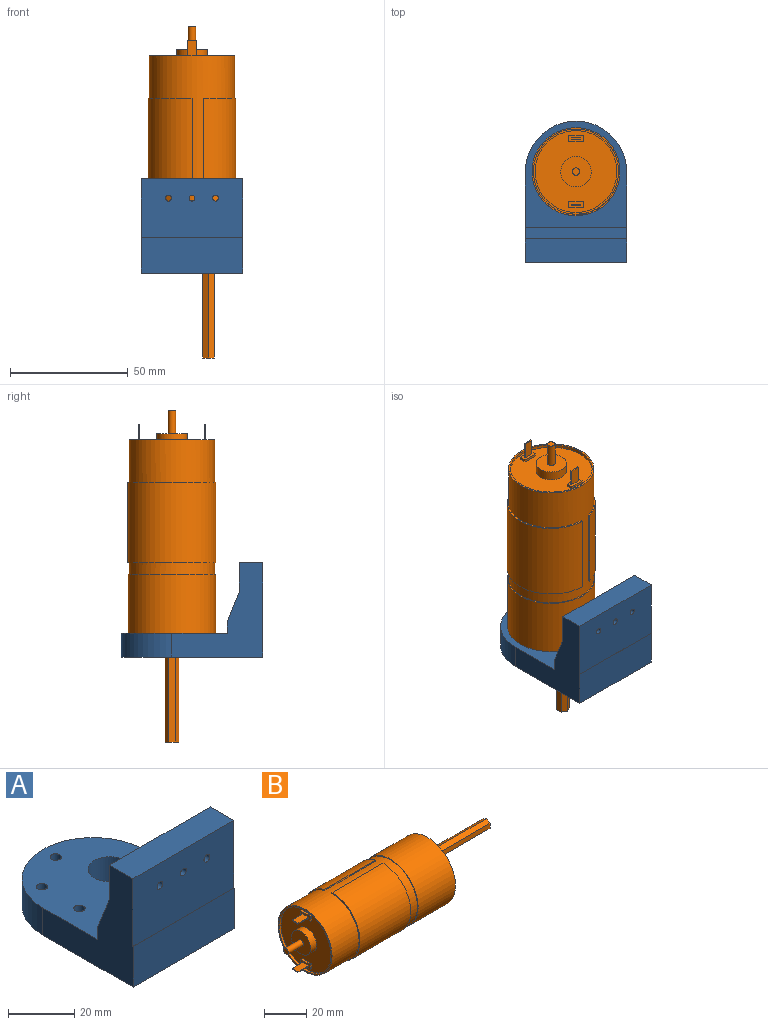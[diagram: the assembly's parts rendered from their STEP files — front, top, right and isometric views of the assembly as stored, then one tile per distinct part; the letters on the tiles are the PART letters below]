
ASSEMBLY  parts=2 mates=1
PART A: 34 faces, bbox 43x60x40 mm
  f0: plane 40x38.5mm, normal (1,0,0), area 741.6mm2, adj f3,f8,f9,f10,f11,f12,f13,f14
  f1: plane 40x38.5mm, normal (-1,0,0), area 741.6mm2, adj f3,f8,f9,f10,f11,f12,f13,f14
  f2: cylinder r=6.5mm len=13mm, axis (0,0,-1), area 408.4mm2, adj f10,f33
  f3: cylinder r=21.5mm len=43mm, axis (0,0,-1), area 675.4mm2, adj f0,f1,f10,f33
  f4: cylinder r=1.7mm len=7mm, axis (0,0,-1), area 74.8mm2, adj f24,f33
  f5: cylinder r=1.7mm len=7mm, axis (0,0,-1), area 74.8mm2, adj f26,f33
  f6: cylinder r=1.7mm len=7mm, axis (0,0,-1), area 74.8mm2, adj f28,f33
  f7: cylinder r=1.7mm len=7mm, axis (0,0,-1), area 74.8mm2, adj f30,f33
  f8: plane 43x0.06mm, normal (0,0,1), area 2.6mm2, adj f0,f1,f9,f11
  f9: plane 43x15mm, normal (0,-1,0), area 645mm2, adj f0,f1,f8,f10
  f10: plane 60x43mm, normal (0,0,-1), area 2116.1mm2, adj f0,f1,f2,f3,f9,f25,f27,f29
  f11: plane 43x25mm, normal (0,-1,0), area 1060.3mm2, adj f0,f1,f8,f13,f15,f18,f21
  f12: plane 43x12.5mm, normal (0,1,0), area 438mm2, adj f0,f1,f13,f14,f17,f20,f23
  f13: plane 43x10mm, normal (0,0,1), area 430mm2, adj f0,f1,f11,f12
  f14: plane 43x12.5mm, normal (0,0.93,0.37), area 578.9mm2, adj f0,f1,f12,f32
  f15: cylinder r=1.25mm len=7mm, axis (0,1,0), area 55mm2, adj f11,f16
  f16: plane 6.5x6.5mm, normal (0,1,0), area 28.3mm2, adj f15,f17
  f17: cylinder r=3.25mm len=6.5mm, axis (0,1,0), area 61.3mm2, adj f12,f16
  f18: cylinder r=1.25mm len=7mm, axis (0,1,0), area 55mm2, adj f11,f19
  f19: plane 6.5x6.5mm, normal (0,1,0), area 28.3mm2, adj f18,f20
  f20: cylinder r=3.25mm len=6.5mm, axis (0,1,0), area 61.3mm2, adj f12,f19
  f21: cylinder r=1.25mm len=7mm, axis (0,1,0), area 55mm2, adj f11,f22
  f22: plane 6.5x6.5mm, normal (0,1,0), area 28.3mm2, adj f21,f23
  f23: cylinder r=3.25mm len=6.5mm, axis (0,1,0), area 61.3mm2, adj f12,f22
  f24: plane 6.5x6.5mm, normal (0,0,-1), area 24.1mm2, adj f4,f25
  f25: cylinder r=3.25mm len=6.5mm, axis (0,0,-1), area 61.3mm2, adj f10,f24
  f26: plane 6.5x6.5mm, normal (0,0,-1), area 24.1mm2, adj f5,f27
  f27: cylinder r=3.25mm len=6.5mm, axis (0,0,-1), area 61.3mm2, adj f10,f26
  f28: plane 6.5x6.5mm, normal (0,0,-1), area 24.1mm2, adj f6,f29
  f29: cylinder r=3.25mm len=6.5mm, axis (0,0,-1), area 61.3mm2, adj f10,f28
  f30: plane 6.5x6.5mm, normal (0,0,-1), area 24.1mm2, adj f7,f31
  f31: cylinder r=3.25mm len=6.5mm, axis (0,0,-1), area 61.3mm2, adj f10,f30
  f32: plane 43x5mm, normal (0,1,0), area 215mm2, adj f0,f1,f14,f33
  f33: plane 44.94x43mm, normal (0,0,1), area 1565mm2, adj f0,f1,f2,f3,f4,f5,f6,f7
PART B: 102 faces, bbox 140.7x37.3x37.3 mm
  f0: cylinder r=18.65mm len=37.3mm, axis (1,0,0), area 3813.7mm2, adj f36,f37,f38,f39
  f1: cylinder r=18.05mm len=57mm, axis (-1,0,0), area 2773.5mm2, adj f36,f37,f38,f39,f40,f41
  f2: cylinder r=17.35mm len=34.7mm, axis (-1,0,0), area 141.7mm2, adj f40,f42
  f3: cylinder r=18.5mm len=37mm, axis (-1,0,0), area 2906mm2, adj f41,f43
  f4: cylinder r=6.45mm len=12.9mm, axis (1,0,0), area 162.1mm2, adj f42,f63
  f5: cylinder r=6mm len=12mm, axis (-1,0,0), area 226.2mm2, adj f43,f66
  f6: cylinder r=1.25mm len=9mm, axis (1,0,0), area 70.7mm2, adj f19,f43
  f7: cylinder r=1.25mm len=9mm, axis (1,0,0), area 70.7mm2, adj f20,f43
  f8: cylinder r=1.25mm len=9mm, axis (1,0,0), area 70.7mm2, adj f21,f43
  f9: cylinder r=1.25mm len=9mm, axis (1,0,0), area 70.7mm2, adj f22,f43
  f10: cylinder r=2.2mm len=4.4mm, axis (1,0,0), area 27.6mm2, adj f43,f67
  f11: cylinder r=2.2mm len=4.4mm, axis (1,0,0), area 27.6mm2, adj f43,f68
  f12: cylinder r=2.2mm len=4.4mm, axis (1,0,0), area 27.6mm2, adj f43,f69
  f13: cylinder r=1.25mm len=2.5mm, axis (1,0,0), area 15.7mm2, adj f23,f43
  f14: cylinder r=1.25mm len=2.5mm, axis (1,0,0), area 15.7mm2, adj f24,f43
  f15: cylinder r=1.25mm len=2.5mm, axis (1,0,0), area 15.7mm2, adj f25,f43
  f16: cylinder r=1.25mm len=2.5mm, axis (1,0,0), area 15.7mm2, adj f26,f43
  f17: cylinder r=1.25mm len=2.5mm, axis (1,0,0), area 15.7mm2, adj f27,f43
  f18: cylinder r=1.25mm len=2.5mm, axis (1,0,0), area 15.7mm2, adj f28,f43
  f19: cone r=1.25mm half-angle=59deg, axis (1,0,0), area 5.7mm2, adj f6
  f20: cone r=1.25mm half-angle=59deg, axis (1,0,0), area 5.7mm2, adj f7
  f21: cone r=1.25mm half-angle=59deg, axis (1,0,0), area 5.7mm2, adj f8
  f22: cone r=1.25mm half-angle=59deg, axis (1,0,0), area 5.7mm2, adj f9
  f23: cone r=1.25mm half-angle=59deg, axis (1,0,0), area 5.7mm2, adj f13
  f24: cone r=1.25mm half-angle=59deg, axis (1,0,0), area 5.7mm2, adj f14
  f25: cone r=1.25mm half-angle=59deg, axis (1,0,0), area 5.7mm2, adj f15
  f26: cone r=1.25mm half-angle=59deg, axis (1,0,0), area 5.7mm2, adj f16
  f27: cone r=1.25mm half-angle=59deg, axis (1,0,0), area 5.7mm2, adj f17
  f28: cone r=1.25mm half-angle=59deg, axis (1,0,0), area 5.7mm2, adj f18
  f29: cylinder r=1.59mm len=10mm, axis (1,0,0), area 99.7mm2, adj f63,f94
  f30: cylinder r=1.2mm len=7mm, axis (1,0,0), area 52.8mm2, adj f33,f67
  f31: cylinder r=1.2mm len=7mm, axis (1,0,0), area 52.8mm2, adj f34,f68
  f32: cylinder r=1.2mm len=7mm, axis (1,0,0), area 52.8mm2, adj f35,f69
  f33: cone r=1.2mm half-angle=59deg, axis (1,0,0), area 5.3mm2, adj f30
  f34: cone r=1.2mm half-angle=59deg, axis (1,0,0), area 5.3mm2, adj f31
  f35: cone r=1.2mm half-angle=59deg, axis (1,0,0), area 5.3mm2, adj f32
  f36: plane 34x0.6mm, normal (0,1,0), area 20.4mm2, adj f0,f1,f37,f38
  f37: plane 37.3x37.3mm, normal (1,0,0), area 66.2mm2, adj f0,f1,f36,f39
  f38: plane 37.3x37.3mm, normal (-1,0,0), area 66.2mm2, adj f0,f1,f36,f39
  f39: plane 34x0.58mm, normal (0,-0.96,0.27), area 20.4mm2, adj f0,f1,f37,f38
  f40: plane 36.1x36.1mm, normal (-1,0,0), area 77.8mm2, adj f1,f2
  f41: plane 37x37mm, normal (-1,0,0), area 51.7mm2, adj f1,f3
  f42: plane 34.7x34.7mm, normal (-1,0,0), area 779.9mm2, adj f2,f4,f44,f45,f46,f47,f48,f49
  f43: plane 37x37mm, normal (1,0,0), area 693.7mm2, adj f3,f5,f6,f7,f8,f9,f10,f11
  f44: plane 6.15x1mm, normal (0,0,1), area 6.2mm2, adj f42,f45,f47,f64
  f45: plane 2.85x1mm, normal (0,1,0), area 2.9mm2, adj f42,f44,f46,f64
  f46: plane 6.15x1mm, normal (0,0,-1), area 6.2mm2, adj f42,f45,f47,f64
  f47: plane 2.85x1mm, normal (0,-1,0), area 2.9mm2, adj f42,f44,f46,f64
  f48: plane 6.15x1mm, normal (0,0,1), area 6.2mm2, adj f42,f49,f51,f65
  f49: plane 2.85x1mm, normal (0,1,0), area 2.9mm2, adj f42,f48,f50,f65
  f50: plane 6.15x1mm, normal (0,0,-1), area 6.2mm2, adj f42,f49,f51,f65
  f51: plane 2.85x1mm, normal (0,-1,0), area 2.9mm2, adj f42,f48,f50,f65
  f52: plane 5.51x0.5mm, normal (0.71,0,0.71), area 3.9mm2, adj f43,f53,f62,f70
  f53: cone r=1mm half-angle=45deg, axis (1,0,0), area 1.1mm2, adj f43,f52,f54,f71
  f54: plane 10.14x5.03mm, normal (0.71,-0.64,-0.3), area 7.7mm2, adj f43,f53,f72,f73
  f55: plane 10.14x5.03mm, normal (0.71,-0.64,0.3), area 7.7mm2, adj f43,f56,f73,f74
  f56: cone r=1mm half-angle=45deg, axis (1,0,0), area 1.1mm2, adj f43,f55,f57,f75
  f57: plane 5.51x0.5mm, normal (0.71,0,-0.71), area 3.9mm2, adj f43,f56,f58,f76
  f58: cone r=1mm half-angle=45deg, axis (1,0,0), area 0.6mm2, adj f43,f57,f59,f77
  f59: plane 10.56x5.22mm, normal (0.71,0.64,-0.3), area 8.1mm2, adj f43,f58,f60,f78
  f60: cone r=1mm half-angle=45deg, axis (1,0,0), area 0.5mm2, adj f43,f59,f61,f79
  f61: plane 10.56x5.22mm, normal (0.71,0.64,0.3), area 8.1mm2, adj f43,f60,f62,f80
  f62: cone r=1mm half-angle=45deg, axis (1,0,0), area 0.6mm2, adj f43,f52,f61,f81
  f63: plane 12.9x12.9mm, normal (-1,0,0), area 122.8mm2, adj f4,f29
  f64: plane 6.15x2.85mm, normal (-1,0,0), area 15.6mm2, adj f44,f45,f46,f47,f82,f83,f95,f97
  f65: plane 6.15x2.85mm, normal (-1,0,0), area 15.6mm2, adj f48,f49,f50,f51,f84,f85,f98,f100
  f66: plane 12x12mm, normal (1,0,0), area 91.4mm2, adj f5,f86,f87,f88,f89,f90,f91
  f67: plane 4.4x4.4mm, normal (1,0,0), area 10.7mm2, adj f10,f30
  f68: plane 4.4x4.4mm, normal (1,0,0), area 10.7mm2, adj f11,f31
  f69: plane 4.4x4.4mm, normal (1,0,0), area 10.7mm2, adj f12,f32
  f70: plane 5.51x0.7mm, normal (0,0,1), area 3.9mm2, adj f52,f71,f81,f92
  f71: cylinder r=0.5mm len=0.71mm, axis (1,0,0), area 0.7mm2, adj f53,f70,f72,f92
  f72: plane 9.93x4.58mm, normal (0,-0.91,-0.42), area 7.7mm2, adj f54,f71,f92,f93
  f73: cone r=0.5mm half-angle=45deg, axis (-1,0,0), area 0.2mm2, adj f54,f55,f93
  f74: plane 9.93x4.58mm, normal (0,-0.91,0.42), area 7.7mm2, adj f55,f75,f92,f93
  f75: cylinder r=0.5mm len=0.71mm, axis (1,0,0), area 0.7mm2, adj f56,f74,f76,f92
  f76: plane 5.51x0.7mm, normal (0,0,-1), area 3.9mm2, adj f57,f75,f77,f92
  f77: cylinder r=0.5mm len=0.7mm, axis (1,0,0), area 0.4mm2, adj f58,f76,f78,f92
  f78: plane 10.35x4.77mm, normal (0,0.91,-0.42), area 8mm2, adj f59,f77,f79,f92
  f79: cylinder r=0.5mm len=0.7mm, axis (1,0,0), area 0.3mm2, adj f60,f78,f80,f92
  f80: plane 10.35x4.77mm, normal (0,0.91,0.42), area 8mm2, adj f61,f79,f81,f92
  f81: cylinder r=0.5mm len=0.7mm, axis (1,0,0), area 0.4mm2, adj f62,f70,f80,f92
  f82: plane 7x3.9mm, normal (0,0,-1), area 27.3mm2, adj f64,f95,f96,f97
  f83: plane 7x3.9mm, normal (0,0,1), area 27.3mm2, adj f64,f95,f96,f97
  f84: plane 7x3.9mm, normal (0,0,-1), area 27.3mm2, adj f65,f98,f99,f100
  f85: plane 7x3.9mm, normal (0,0,1), area 27.3mm2, adj f65,f98,f99,f100
  f86: plane 40x2.5mm, normal (0,0.5,0.87), area 115.5mm2, adj f66,f87,f91,f101
  f87: plane 40x2.5mm, normal (0,-0.5,0.87), area 115.5mm2, adj f66,f86,f88,f101
  f88: plane 40x2.89mm, normal (0,-1,0), area 115.5mm2, adj f66,f87,f89,f101
  f89: plane 40x2.5mm, normal (0,-0.5,-0.87), area 115.5mm2, adj f66,f88,f90,f101
  f90: plane 40x2.5mm, normal (0,0.5,-0.87), area 115.5mm2, adj f66,f89,f91,f101
  f91: plane 40x2.89mm, normal (0,1,0), area 115.5mm2, adj f66,f86,f90,f101
  f92: plane 21.7x11.28mm, normal (1,0,0), area 143mm2, adj f70,f71,f72,f74,f75,f76,f77,f78
  f93: cylinder r=0.5mm len=0.7mm, axis (1,0,0), area 0.3mm2, adj f72,f73,f74,f92
  f94: plane 3.18x3.18mm, normal (-1,0,0), area 7.9mm2, adj f29
  f95: plane 7x0.5mm, normal (0,-1,0), area 3.5mm2, adj f64,f82,f83,f96
  f96: plane 3.9x0.5mm, normal (-1,0,0), area 2mm2, adj f82,f83,f95,f97
  f97: plane 7x0.5mm, normal (0,1,0), area 3.5mm2, adj f64,f82,f83,f96
  f98: plane 7x0.5mm, normal (0,-1,0), area 3.5mm2, adj f65,f84,f85,f99
  f99: plane 3.9x0.5mm, normal (-1,0,0), area 2mm2, adj f84,f85,f98,f100
  f100: plane 7x0.5mm, normal (0,1,0), area 3.5mm2, adj f65,f84,f85,f99
  f101: plane 5.77x5mm, normal (1,0,0), area 21.7mm2, adj f86,f87,f88,f89,f90,f91
PLACE A t=(-36.03,-4.03,-7.59)mm fixed
PLACE B rot(axis=(0.58,0.58,-0.58),120deg) t=(-22.17,3.97,84.41)mm
MATE revolute B.f8 <-> A.f4  axis (0,0,-1) through (-22.17,19.97,2.41)mm
